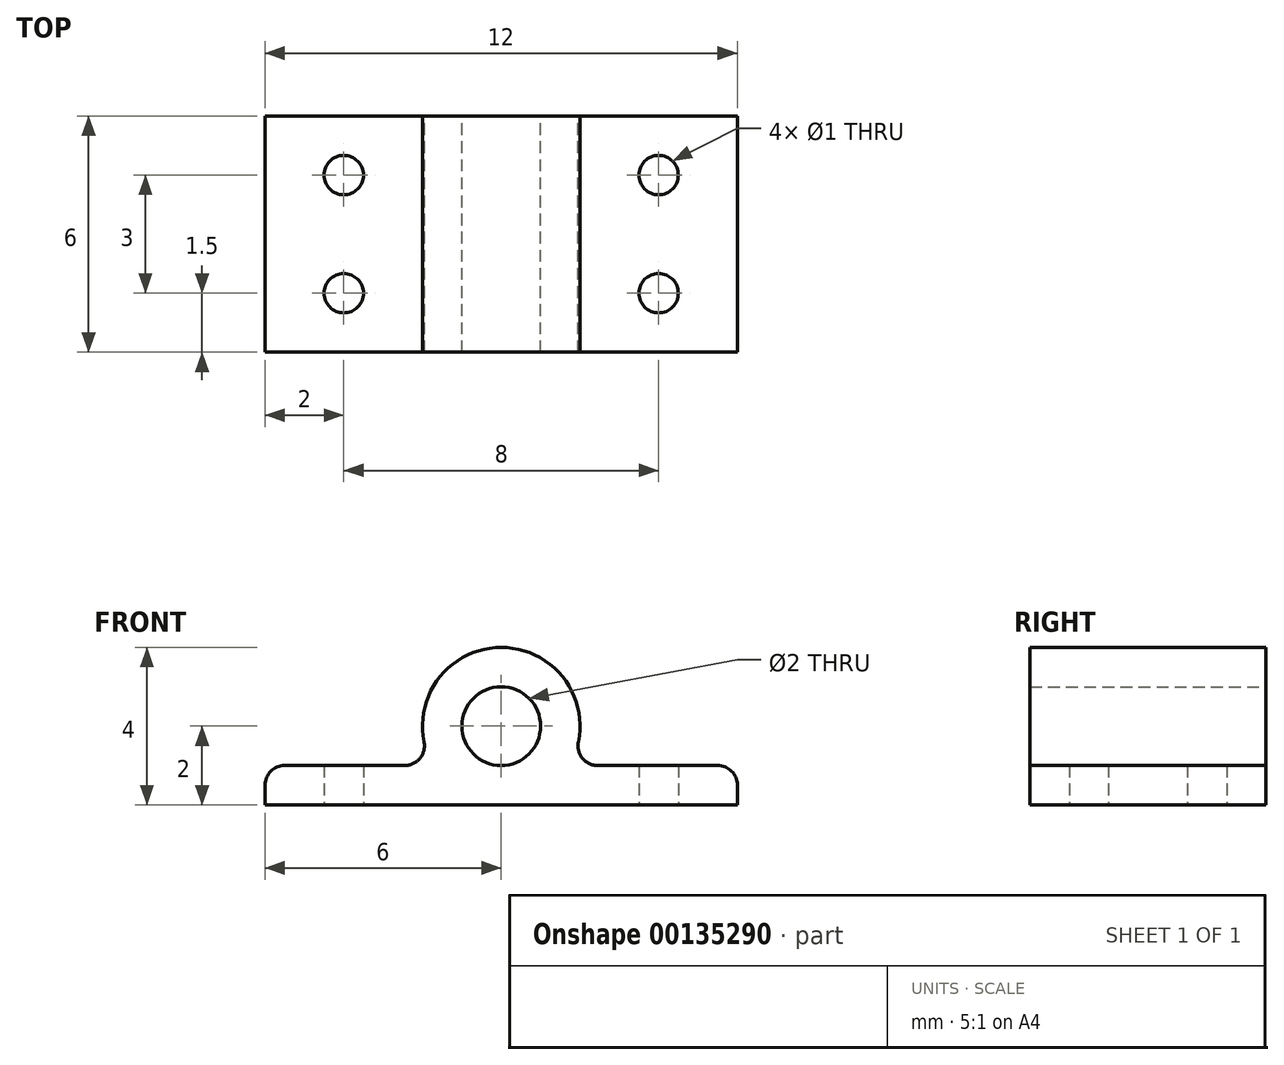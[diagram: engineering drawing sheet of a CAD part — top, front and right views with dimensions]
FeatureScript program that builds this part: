
annotation { "Feature Type Name" : "Feature", "Feature Type Description" : "" }
export const myFeature = defineFeature(function(context is Context, id is Id, definition is map)
    precondition{}
    {
        {
            var Q0;
            Q0=qCreatedBy(makeId("Front.planeOp"),FACE);
            var sketch = newSketch(context, id + "F0", { "sketchPlane" : qUnion([Q0])});
            skLineSegment(sketch, "E0", {"start": v(0, 0) * mm, "end": v(-12, 0) * mm});
            skLineSegment(sketch, "E1", {"start": v(-12, 0) * mm, "end": v(-12, 1) * mm});
            skLineSegment(sketch, "E2", {"start": v(-12, 1) * mm, "end": v(-7.73, 1) * mm});
            skArc(sketch, "E3", {"start": v(-4.27, 1) * mm, "mid": v(-6, 4) * mm, "end": v(-7.73, 1) * mm});
            skCircle(sketch, "E4", {"center": v(-6, 2) * mm, "radius": 1 * mm});
            skLineSegment(sketch, "E5.trimOffspring", {"start": v(-4.27, 1) * mm, "end": v(0, 1) * mm});
            skLineSegment(sketch, "E6", {"start": v(0, 1) * mm, "end": v(0, 0) * mm});
            skSolve(sketch);
        }
        {
            var Q0;
            Q0 = qSketchRegion(id + "F0", true);
            extrude(context, id + "F1", {"entities" : qUnion([Q0]), "depth" : 6 * mm});
        }
        {
            var Q0;
            Q0=makeQuery(id+"F1.opExtrude","SWEPT_FACE",FACE,{"disambiguationData":[OSD([sQuery(id+"F0.wireOp",EDGE,"E0")])]});
            var sketch = newSketch(context, id + "F2", { "sketchPlane" : qUnion([Q0])});
            skCircle(sketch, "E7", {"center": v(-2, 1.5) * mm, "radius": 0.5 * mm});
            skCircle(sketch, "E8", {"center": v(-10, 1.5) * mm, "radius": 0.5 * mm});
            skCircle(sketch, "E9", {"center": v(-10, 4.5) * mm, "radius": 0.5 * mm});
            skCircle(sketch, "E10", {"center": v(-2, 4.5) * mm, "radius": 0.5 * mm});
            skSolve(sketch);
        }
        {
            var Q0;
            Q0 = qSketchRegion(id + "F2", true);
            extrude(context, id + "F3", {"entities" : qUnion([Q0]), "operationType" : NewBodyOperationType.REMOVE, "endBound" : BoundingType.THROUGH_ALL, "oppositeDirection" : true, "depth" : 25 * mm});
        }
        {
            var Q0;
            Q0=makeQuery(id+"F1.opExtrude","SWEPT_EDGE",EDGE,{"disambiguationData":[OSD([sQuery(id+"F0.wireOp",EDGE,"E1"),sQuery(id+"F0.wireOp",EDGE,"E2")])]});
            var Q1;
            Q1=makeQuery(id+"F1.opExtrude","SWEPT_EDGE",EDGE,{"disambiguationData":[OSD([sQuery(id+"F0.wireOp",EDGE,"E5.trimOffspring"),sQuery(id+"F0.wireOp",EDGE,"E6")])]});
            var Q2;
            Q2=makeQuery(id+"F1.opExtrude","SWEPT_EDGE",EDGE,{"disambiguationData":[OSD([sQuery(id+"F0.wireOp",EDGE,"E3"),sQuery(id+"F0.wireOp",EDGE,"E5.trimOffspring")])]});
            var Q3;
            Q3=makeQuery(id+"F1.opExtrude","SWEPT_EDGE",EDGE,{"disambiguationData":[OSD([sQuery(id+"F0.wireOp",EDGE,"E2"),sQuery(id+"F0.wireOp",EDGE,"E3")])]});
            fillet(context, id + "F4", {"entities" : qUnion([Q0, Q1, Q2, Q3]), "radius" : 0.5 * mm, "tangentPropagation" : true, "allowEdgeOverflow" : false});
        }
    });
